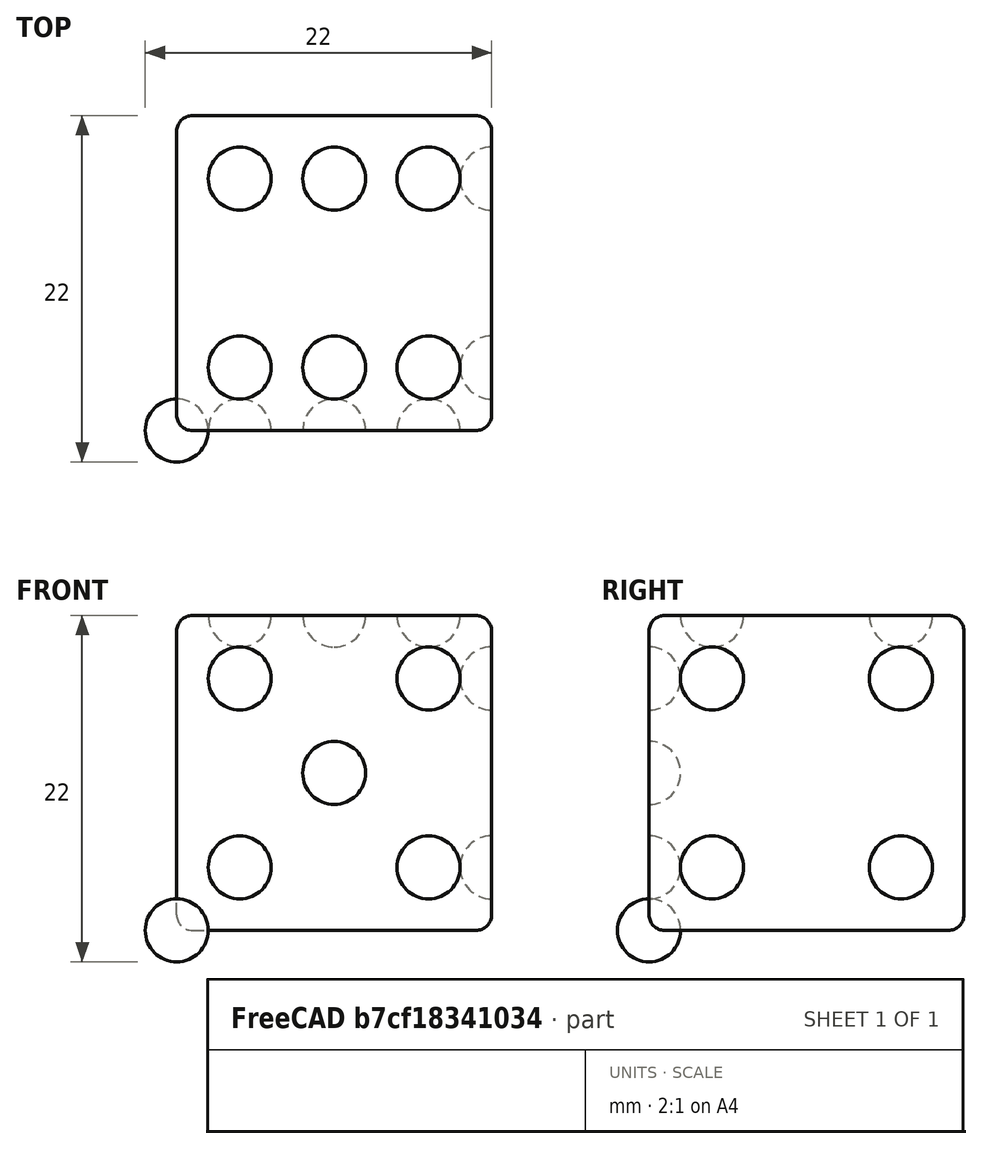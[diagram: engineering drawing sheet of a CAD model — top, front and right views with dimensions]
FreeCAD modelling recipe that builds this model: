
FCSTD DOCUMENT  (FreeCAD 0.21R33694 (Git))
Label: OJT1_T13R02_dau
License: All rights reserved
LicenseURL: http://en.wikipedia.org/wiki/All_rights_reserved
objects: Part::Sphere×4, Part::Cut×4, Part::FeaturePython×3, Part::Box×1, Part::Fillet×1
note: 10 computed .brp shape members not serialized (recipe doc carries the construction recipe); baked Part::Feature solids carry a one-line shape summary decoded from their .brp

FEATURE [Part::Box] Box  label="Cube"
  AttacherType = Attacher::AttachEngine3D
  Height = 20
  Length = 20
  Width = 20
FEATURE [Part::Sphere] Sphere
  Angle1 = -90
  Angle2 = 90
  Angle3 = 360
  AttacherType = Attacher::AttachEngine3D
  Radius = 2
FEATURE [Part::FeaturePython] Array  label="numero6"  # Draft array (typed FeaturePython)
  AlwaysSyncPlacement = false
  Angle = 360
  ArrayType = 0
  Axis = (0,0,1)
  Base = -> Sphere
  Center = (0,0,0)
  Count = 6
  ExpandArray = false
  Fuse = false
  IntervalAxis = (0,0,0)
  IntervalX = (6,0,0)
  IntervalY = (0,12,0)
  IntervalZ = (0,0,100)
  NumberCircles = 3
  NumberPolar = 5
  NumberX = 3
  NumberY = 2
  NumberZ = 1
  Placement = pos=(4,4,20) rot=(0,0,1;0rad)
  PlacementList = 6 placements: [(0,0,0),(0,12,0),(6,0,0),(6,12,0),(12,0,0),(12,12,0)]
  RadialDistance = 50
  ScaleList = (6) [(1,1,1),(1,1,1),(1,1,1),(1,1,1),(1,1,1),(1,1,1)]
  Symmetry = 1
  TangentialDistance = 25
FEATURE [Part::Sphere] Sphere001
  Angle1 = -90
  Angle2 = 90
  Angle3 = 360
  AttacherType = Attacher::AttachEngine3D
  Radius = 2
FEATURE [Part::FeaturePython] Array001  label="numero4"  # Draft array (typed FeaturePython)
  AlwaysSyncPlacement = false
  Angle = 360
  ArrayType = 0
  Axis = (0,0,1)
  Base = -> Sphere001
  Center = (0,0,0)
  Count = 4
  ExpandArray = false
  Fuse = false
  IntervalAxis = (0,0,0)
  IntervalX = (12,0,0)
  IntervalY = (0,12,0)
  IntervalZ = (0,0,100)
  NumberCircles = 3
  NumberPolar = 5
  NumberX = 2
  NumberY = 2
  NumberZ = 1
  Placement = pos=(20,4,17) rot=(0,1,0;1.5708rad)
  PlacementList = 4 placements: [(0,0,0),(0,12,0),(12,0,0),(12,12,0)]
  RadialDistance = 50
  ScaleList = (4) [(1,1,1),(1,1,1),(1,1,1),(1,1,1)]
  Symmetry = 1
  TangentialDistance = 25
FEATURE [Part::Sphere] Sphere002
  Angle1 = -90
  Angle2 = 90
  Angle3 = 360
  AttacherType = Attacher::AttachEngine3D
  Radius = 2
FEATURE [Part::FeaturePython] Array002  label="numero5"  # Draft array (typed FeaturePython)
  AlwaysSyncPlacement = false
  Angle = 360
  ArrayType = 0
  Axis = (0,0,1)
  Base = -> Sphere002
  Center = (0,0,0)
  Count = 4
  ExpandArray = false
  Fuse = false
  IntervalAxis = (0,0,0)
  IntervalX = (12,0,0)
  IntervalY = (0,12,0)
  IntervalZ = (0,0,100)
  NumberCircles = 3
  NumberPolar = 5
  NumberX = 2
  NumberY = 2
  NumberZ = 1
  Placement = pos=(4,0,16) rot=(0.57735,0.57735,-0.57735;2.0944rad)
  PlacementList = 4 placements: [(0,0,0),(0,12,0),(12,0,0),(12,12,0)]
  RadialDistance = 50
  ScaleList = (4) [(1,1,1),(1,1,1),(1,1,1),(1,1,1)]
  Symmetry = 1
  TangentialDistance = 25
FEATURE [Part::Sphere] Sphere003
  Angle1 = -90
  Angle2 = 90
  Angle3 = 360
  AttacherType = Attacher::AttachEngine3D
  Placement = pos=(10,0,10) rot=(0,0,1;0rad)
  Radius = 2
FEATURE [Part::Cut] Cut
  Base = -> Box
  Refine = true
  Tool = -> Array
FEATURE [Part::Cut] Cut001
  Base = -> Cut
  Refine = true
  Tool = -> Sphere003
FEATURE [Part::Cut] Cut002
  Base = -> Cut001
  Refine = true
  Tool = -> Array002
FEATURE [Part::Cut] Cut003
  Base = -> Cut002
  Refine = true
  Tool = -> Array001
FEATURE [Part::Fillet] Fillet
  Base = -> Cut003
  Edges = 12 edges r=1: [Edge1,Edge2,Edge3,Edge4,Edge5,Edge6,Edge7,Edge14,Edge15,Edge22,Edge23,Edge24]
